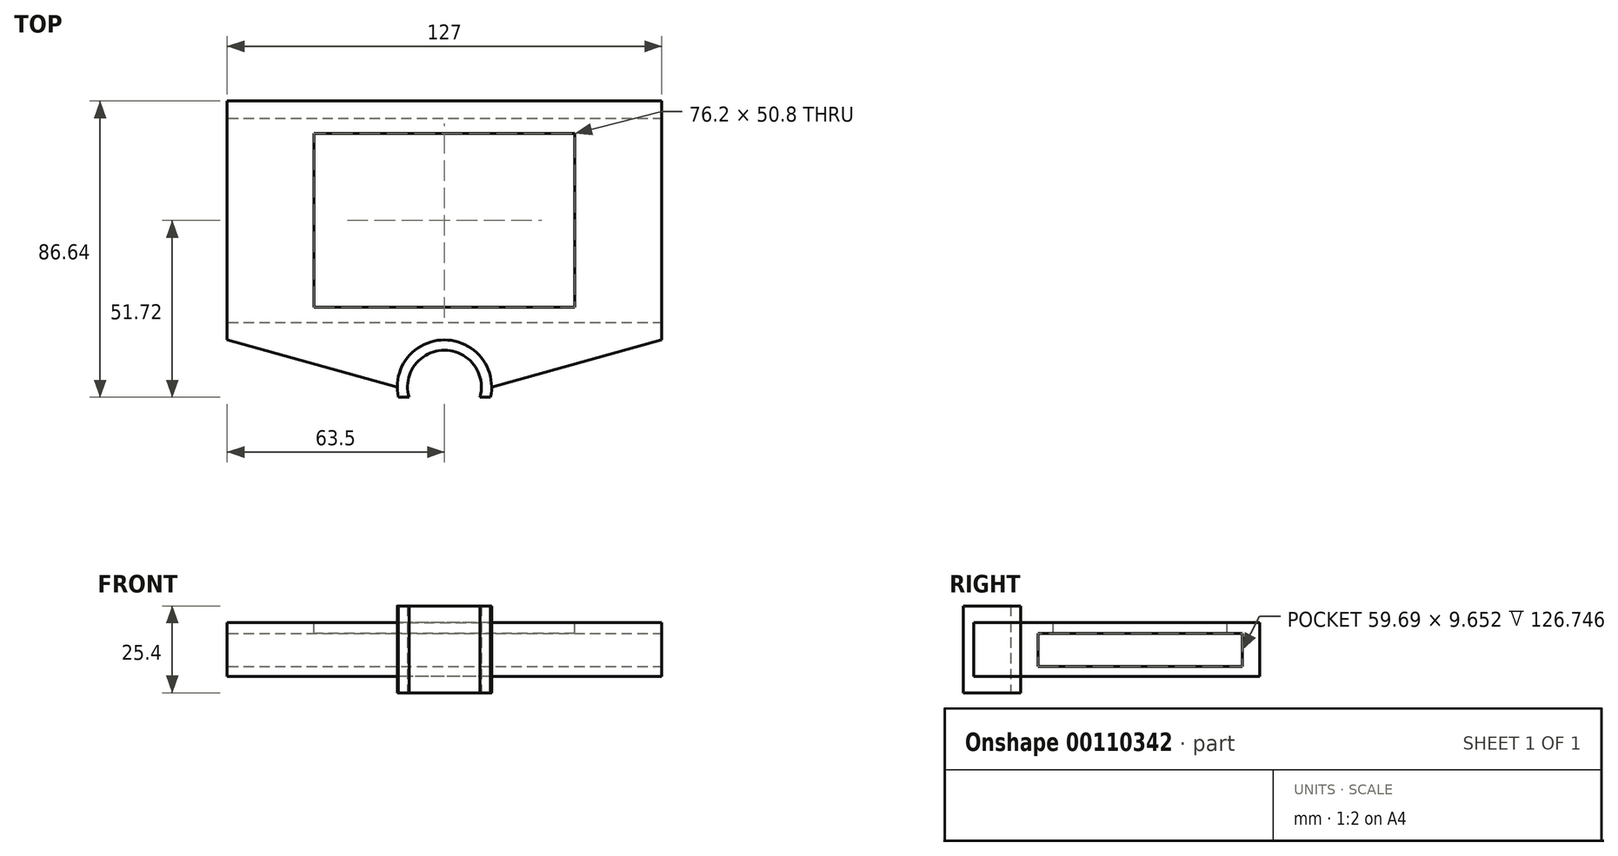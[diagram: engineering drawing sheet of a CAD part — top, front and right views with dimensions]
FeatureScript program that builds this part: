
annotation { "Feature Type Name" : "Feature", "Feature Type Description" : "" }
export const myFeature = defineFeature(function(context is Context, id is Id, definition is map)
    precondition{}
    {
        {
            var Q0;
            Q0=qCreatedBy(makeId("Top.planeOp"),FACE);
            var sketch = newSketch(context, id + "F0", { "sketchPlane" : qUnion([Q0])});
            skArc(sketch, "E0", {"start": v(10.37, -3) * mm, "mid": v(0, 10.8) * mm, "end": v(-10.37, -3) * mm});
            skPoint(sketch, "E1", {"position": v(-10.8, 0) * mm});
            skPoint(sketch, "E2", {"position": v(-10.37, -3) * mm});
            skPoint(sketch, "E3.positionSnap0", {"position": v(0, -3) * mm});
            skPoint(sketch, "E4", {"position": v(-13.8, 0) * mm});
            skArc(sketch, "E5", {"start": v(13.8, 0) * mm, "mid": v(0, 13.8) * mm, "end": v(-13.8, 0) * mm});
            skPoint(sketch, "E6", {"position": v(10.8, 0) * mm});
            skArc(sketch, "E7", {"start": v(13.46, -3) * mm, "mid": v(0, 13.8) * mm, "end": v(-13.46, -3) * mm});
            skLineSegment(sketch, "E8", {"start": v(-13.46, -3) * mm, "end": v(-10.37, -3) * mm});
            skLineSegment(sketch, "E9", {"start": v(10.37, -3) * mm, "end": v(13.46, -3) * mm});
            skPoint(sketch, "E10", {"position": v(0, 13.8) * mm});
            skSolve(sketch);
        }
        {
            var Q0;
            Q0 = qSketchRegion(id + "F0", true);
            extrude(context, id + "F1", {"entities" : qUnion([Q0]), "endBound" : BoundingType.SYMMETRIC, "depth" : 25.4 * mm});
        }
        {
            var Q0;
            Q0=qCreatedBy(makeId("Top.planeOp"),FACE);
            var sketch = newSketch(context, id + "F2", { "sketchPlane" : qUnion([Q0])});
            skPoint(sketch, "E11.middle", {"position": v(0, 43.4) * mm});
            skPoint(sketch, "E12", {"position": v(0, 13.8) * mm});
            skPoint(sketch, "E13", {"position": v(-60.5, 16.8) * mm});
            skPoint(sketch, "E14", {"position": v(-63.5, 16.8) * mm});
            skPoint(sketch, "E15", {"position": v(63.5, 77.64) * mm});
            skPoint(sketch, "E16", {"position": v(-60.5, 13.8) * mm});
            skPoint(sketch, "E17", {"position": v(60.5, 83.64) * mm});
            skPoint(sketch, "E18", {"position": v(-63.5, 13.8) * mm});
            skPoint(sketch, "E19", {"position": v(63.5, 83.64) * mm});
            skLineSegment(sketch, "E20.bottom", {"start": v(63.5, 83.64) * mm, "end": v(-63.5, 83.64) * mm});
            skLineSegment(sketch, "E20.left", {"start": v(63.5, 83.64) * mm, "end": v(63.5, 13.8) * mm});
            skLineSegment(sketch, "E20.right", {"start": v(-63.5, 83.64) * mm, "end": v(-63.5, 13.8) * mm});
            skLineSegment(sketch, "E21", {"start": v(-63.5, 13.8) * mm, "end": v(-13.8, 0) * mm});
            skLineSegment(sketch, "E22", {"start": v(63.5, 13.8) * mm, "end": v(13.8, 0) * mm});
            skLineSegment(sketch, "E23.trimOffspring", {"start": v(-60.5, 13.8) * mm, "end": v(-63.5, 13.8) * mm});
            skArc(sketch, "E24", {"start": v(13.8, 0) * mm, "mid": v(0, 13.8) * mm, "end": v(-13.8, 0) * mm});
            skSolve(sketch);
        }
        {
            var Q0;
            Q0 = qSketchRegion(id + "F2", true);
            extrude(context, id + "F3", {"entities" : qUnion([Q0]), "endBound" : BoundingType.SYMMETRIC, "depth" : 15.7 * mm});
        }
        {
            var Q0;
            Q0=makeQuery(id+"F3.opExtrude","SWEPT_FACE",FACE,{"disambiguationData":[OSD([sQuery(id+"F2.wireOp",EDGE,"E20.left")])]});
            var sketch = newSketch(context, id + "F4", { "sketchPlane" : qUnion([Q0])});
            skLineSegment(sketch, "E25.bottom", {"start": v(18.87, -5.02) * mm, "end": v(78.56, -5.02) * mm});
            skLineSegment(sketch, "E25.top", {"start": v(18.87, 4.63) * mm, "end": v(78.56, 4.63) * mm});
            skLineSegment(sketch, "E25.left", {"start": v(18.87, -5.02) * mm, "end": v(18.87, 4.63) * mm});
            skLineSegment(sketch, "E25.right", {"start": v(78.56, -5.02) * mm, "end": v(78.56, 4.63) * mm});
            skPoint(sketch, "E26", {"position": v(48.72, 4.63) * mm});
            skPoint(sketch, "E27", {"position": v(48.72, 7.85) * mm});
            skPoint(sketch, "E28", {"position": v(78.56, -0.2) * mm});
            skPoint(sketch, "E29", {"position": v(83.64, 0) * mm});
            skSolve(sketch);
        }
        {
            var Q0;
            Q0 = qSketchRegion(id + "F4", true);
            extrude(context, id + "F5", {"entities" : qUnion([Q0]), "operationType" : NewBodyOperationType.REMOVE, "endBound" : BoundingType.THROUGH_ALL, "oppositeDirection" : true, "depth" : 25.4 * mm});
        }
        {
            var Q0;
            Q0=makeQuery(id+"F3.opExtrude","CAP_FACE",FACE,{"disambiguationData":[OSD([sQuery(id+"F2.wireOp",EDGE,"E20.bottom"),sQuery(id+"F2.wireOp",EDGE,"E20.left"),sQuery(id+"F2.wireOp",EDGE,"E20.right"),sQuery(id+"F2.wireOp",EDGE,"E21"),sQuery(id+"F2.wireOp",EDGE,"E22"),sQuery(id+"F2.wireOp",EDGE,"E24")])],"isStart":false});
            var sketch = newSketch(context, id + "F6", { "sketchPlane" : qUnion([Q0])});
            skLineSegment(sketch, "E30.bottom", {"start": v(-38.1, 74.12) * mm, "end": v(38.1, 74.12) * mm});
            skLineSegment(sketch, "E30.top", {"start": v(-38.1, 23.32) * mm, "end": v(38.1, 23.32) * mm});
            skLineSegment(sketch, "E30.left", {"start": v(-38.1, 74.12) * mm, "end": v(-38.1, 23.32) * mm});
            skLineSegment(sketch, "E30.right", {"start": v(38.1, 74.12) * mm, "end": v(38.1, 23.32) * mm});
            skPoint(sketch, "E31", {"position": v(0, 83.64) * mm});
            skPoint(sketch, "E32", {"position": v(63.5, 48.72) * mm});
            skPoint(sketch, "E33", {"position": v(0, 74.12) * mm});
            skPoint(sketch, "E34", {"position": v(38.1, 48.72) * mm});
            skSolve(sketch);
        }
        {
            var Q0;
            Q0 = qSketchRegion(id + "F6", true);
            extrude(context, id + "F7", {"entities" : qUnion([Q0]), "operationType" : NewBodyOperationType.REMOVE, "oppositeDirection" : true, "depth" : 5.08 * mm});
        }
        {
            var Q0;
            Q0=makeQuery(id+"F3.opExtrude","SWEPT_FACE",FACE,{"disambiguationData":[OSD([sQuery(id+"F2.wireOp",EDGE,"E20.right")])]});
            var sketch = newSketch(context, id + "F8", { "sketchPlane" : qUnion([Q0])});
            skSolve(sketch);
        }
        {
            var Q0;
            {var subQ0=sQuery(id+"F2.wireOp",EDGE,"E20.right");Q0=makeQuery(id+"F8.imprint","IMPRINT",FACE,{"disambiguationData":[TD([[makeQuery(id+"F8.imprint","IMPRINT",EDGE,{"derivedFrom":makeQuery(id+"F3.opExtrude","CAP_EDGE",EDGE,{"disambiguationData":[OSD([subQ0])],"isStart":true})}),1.0]])]});}
            var sketch = newSketch(context, id + "F9", { "sketchPlane" : qUnion([Q0])});
            skLineSegment(sketch, "E35.bottom", {"start": v(-17.69, 5.56) * mm, "end": v(-80.1, 5.56) * mm});
            skLineSegment(sketch, "E35.top", {"start": v(-17.69, -5.59) * mm, "end": v(-80.1, -5.59) * mm});
            skLineSegment(sketch, "E35.left", {"start": v(-17.69, 5.56) * mm, "end": v(-17.69, -5.59) * mm});
            skLineSegment(sketch, "E35.right", {"start": v(-80.1, 5.56) * mm, "end": v(-80.1, -5.59) * mm});
            skSolve(sketch);
        }
        {
            var Q0;
            Q0 = qSketchRegion(id + "F9", true);
            extrude(context, id + "F10", {"entities" : qUnion([Q0]), "operationType" : NewBodyOperationType.ADD, "oppositeDirection" : true, "depth" : 0.25 * mm});
        }
    });
